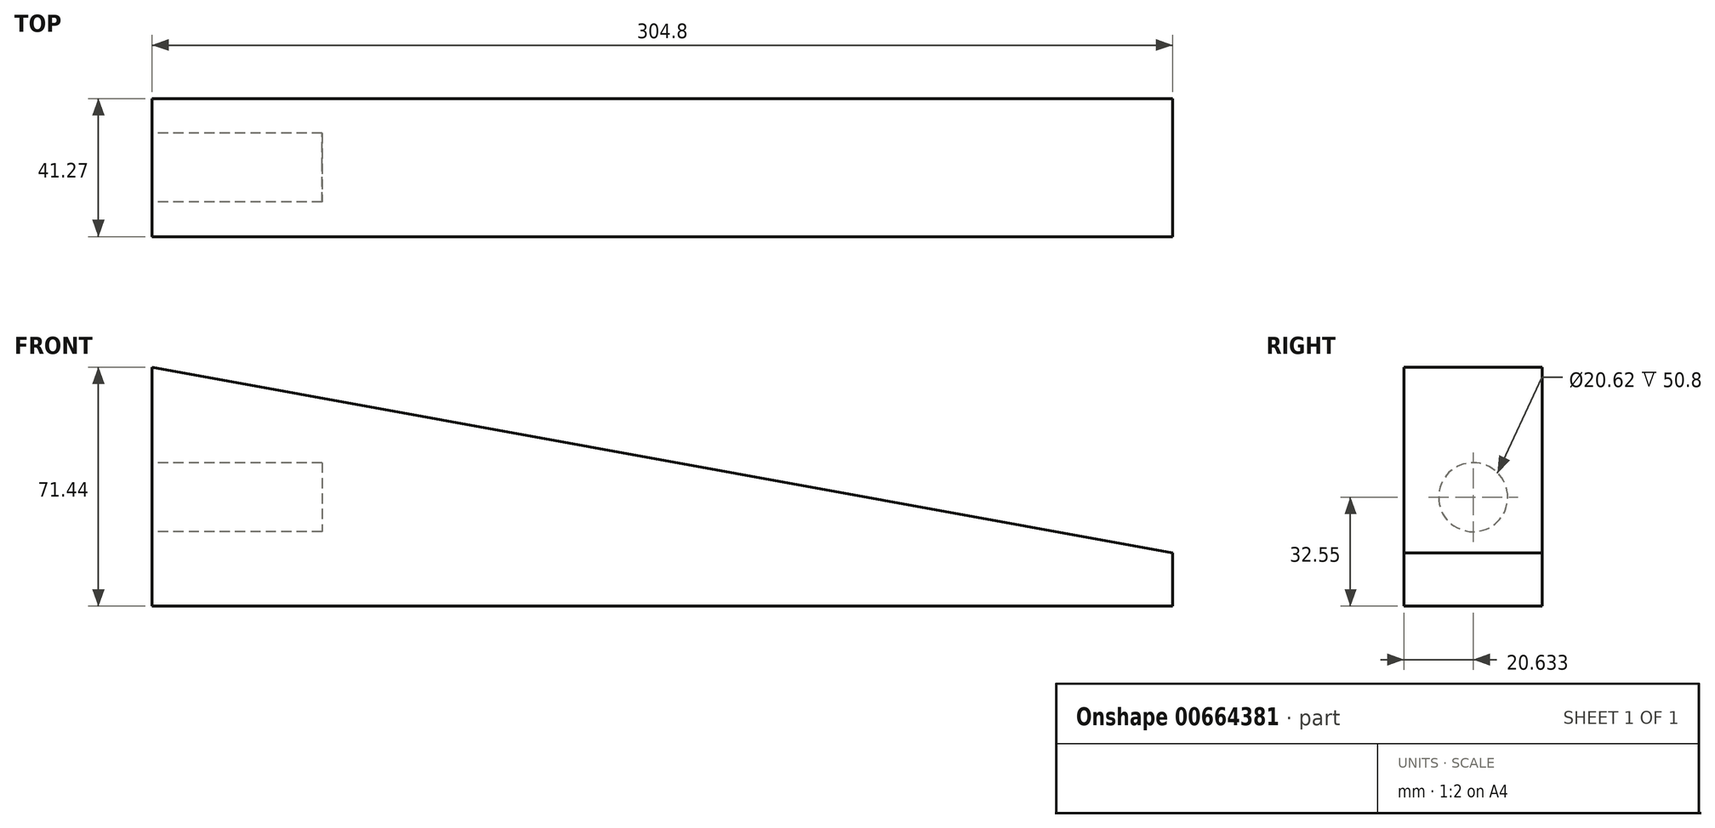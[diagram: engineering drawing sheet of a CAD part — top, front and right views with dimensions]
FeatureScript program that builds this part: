
annotation { "Feature Type Name" : "Feature", "Feature Type Description" : "" }
export const myFeature = defineFeature(function(context is Context, id is Id, definition is map)
    precondition{}
    {
        {
            var Q0;
            Q0=qCreatedBy(makeId("Front.planeOp"),FACE);
            var sketch = newSketch(context, id + "F0", { "sketchPlane" : qUnion([Q0])});
            skLineSegment(sketch, "E0", {"start": v(0, 0) * mm, "end": v(0, 71.44) * mm});
            skLineSegment(sketch, "E1", {"start": v(0, 0) * mm, "end": v(304.8, 0) * mm});
            skLineSegment(sketch, "E2", {"start": v(304.8, 0) * mm, "end": v(304.8, 15.88) * mm});
            skLineSegment(sketch, "E3", {"start": v(0, 71.44) * mm, "end": v(304.8, 15.88) * mm});
            skSolve(sketch);
        }
        {
            var Q0;
            Q0=makeQuery(id+"F0.imprint","IMPRINT",FACE,{"disambiguationData":[TD([[makeQuery(id+"F0.imprint","IMPRINT",EDGE,{"derivedFrom":sQuery(id+"F0.wireOp",EDGE,"E0")}),-1.0]])]});
            extrude(context, id + "F1", {"entities" : qUnion([Q0]), "depth" : 41.27 * mm, "offsetDistance" : 25.4 * mm});
        }
        {
            var Q0;
            Q0=makeQuery(id+"F1.opExtrude","SWEPT_FACE",FACE,{"disambiguationData":[OSD([sQuery(id+"F0.wireOp",EDGE,"E0")])]});
            var sketch = newSketch(context, id + "F2", { "sketchPlane" : qUnion([Q0])});
            skPoint(sketch, "E4.endSnap0", {"position": v(20.64, 71.44) * mm});
            skCircle(sketch, "E5", {"center": v(20.64, 32.55) * mm, "radius": 10.31 * mm});
            skSolve(sketch);
        }
        {
            var Q0;
            Q0=makeQuery(id+"F2.imprint","IMPRINT",FACE,{"disambiguationData":[TD([[makeQuery(id+"F2.imprint","IMPRINT",EDGE,{"derivedFrom":sQuery(id+"F2.wireOp",EDGE,"E5")}),1.0]])]});
            extrude(context, id + "F3", {"entities" : qUnion([Q0]), "operationType" : NewBodyOperationType.REMOVE, "oppositeDirection" : true, "depth" : 50.8 * mm, "offsetDistance" : 25.4 * mm});
        }
    });
